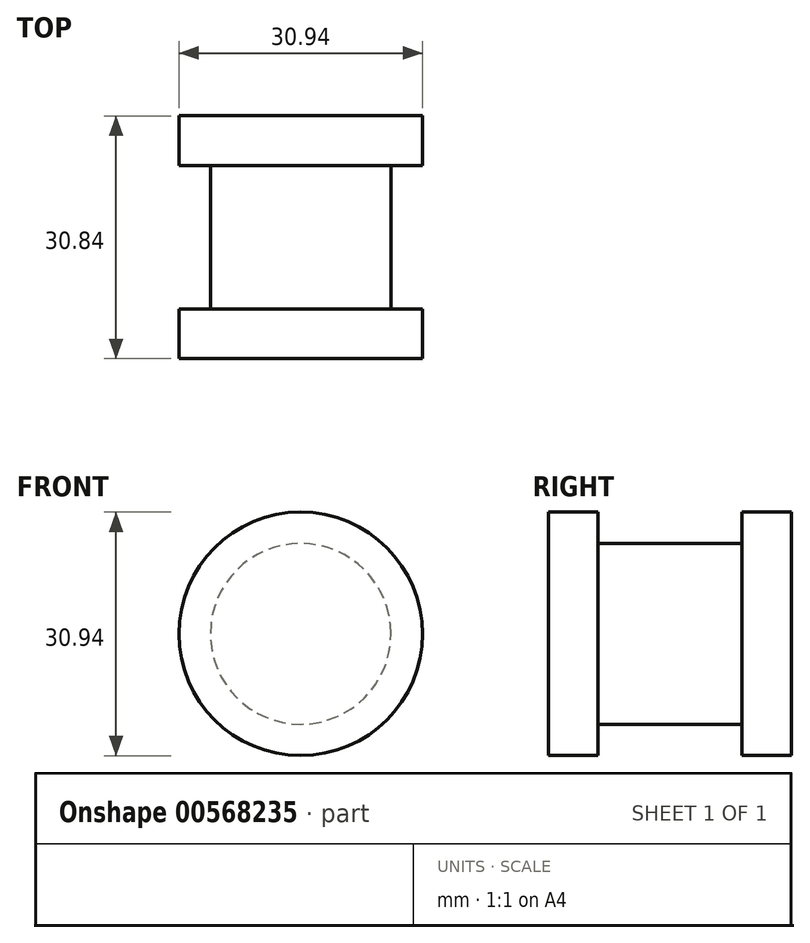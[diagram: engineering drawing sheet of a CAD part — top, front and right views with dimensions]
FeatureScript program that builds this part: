
annotation { "Feature Type Name" : "Feature", "Feature Type Description" : "" }
export const myFeature = defineFeature(function(context is Context, id is Id, definition is map)
    precondition{}
    {
        {
            var Q0;
            Q0=qCreatedBy(makeId("Right.planeOp"),FACE);
            var sketch = newSketch(context, id + "F0", { "sketchPlane" : qUnion([Q0])});
            skLineSegment(sketch, "E0", {"start": v(-15.42, 16.97) * mm, "end": v(-9.13, 16.97) * mm});
            skLineSegment(sketch, "E1", {"start": v(-9.13, 16.97) * mm, "end": v(-9.13, 12.98) * mm});
            skLineSegment(sketch, "E2", {"start": v(-9.13, 12.98) * mm, "end": v(0, 12.98) * mm});
            skLineSegment(sketch, "E3.MirrorCS", {"start": v(15.42, 16.97) * mm, "end": v(9.13, 16.97) * mm});
            skLineSegment(sketch, "E4.MirrorCS", {"start": v(9.13, 16.97) * mm, "end": v(9.13, 12.98) * mm});
            skLineSegment(sketch, "E5.MirrorCS", {"start": v(9.13, 12.98) * mm, "end": v(0, 12.98) * mm});
            skLineSegment(sketch, "E6", {"start": v(-15.42, 16.97) * mm, "end": v(-15.42, 1.5) * mm});
            skLineSegment(sketch, "E7.MirrorCS", {"start": v(15.42, 16.97) * mm, "end": v(15.42, 1.5) * mm});
            skLineSegment(sketch, "E8", {"start": v(-15.42, 1.5) * mm, "end": v(15.42, 1.5) * mm});
            skSolve(sketch);
        }
        {
            var Q0;
            Q0=makeQuery(id+"F0.imprint","IMPRINT",FACE,{"disambiguationData":[TD([[makeQuery(id+"F0.imprint","IMPRINT",EDGE,{"derivedFrom":sQuery(id+"F0.wireOp",EDGE,"E0")}),-1.0]])]});
            var Q1;
            Q1=sQuery(id+"F0.wireOp",EDGE,"E8");
            revolve(context, id + "F1", {"entities" : qUnion([Q0]), "axis" : qUnion([Q1]), "revolveType" : RevolveType.FULL});
        }
    });
